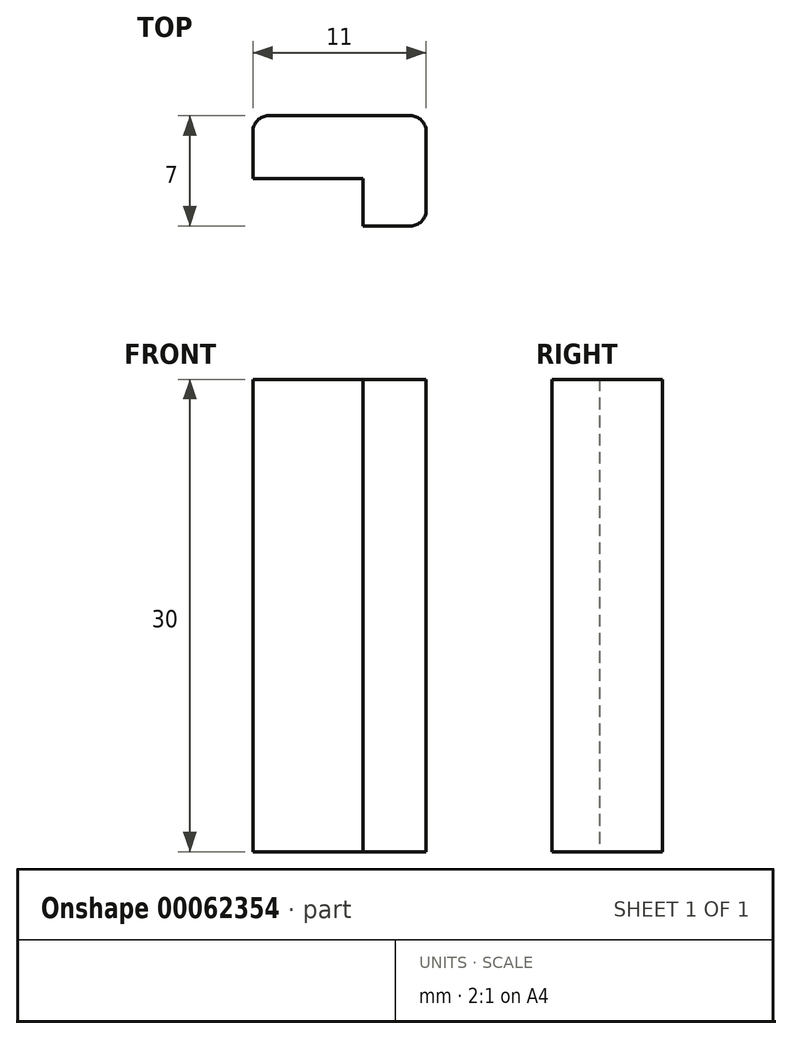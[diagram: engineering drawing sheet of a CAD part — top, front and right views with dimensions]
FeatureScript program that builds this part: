
annotation { "Feature Type Name" : "Feature", "Feature Type Description" : "" }
export const myFeature = defineFeature(function(context is Context, id is Id, definition is map)
    precondition{}
    {
        {
            var Q0;
            Q0=qCreatedBy(makeId("Top.planeOp"),FACE);
            var sketch = newSketch(context, id + "F0", { "sketchPlane" : qUnion([Q0])});
            skLineSegment(sketch, "E0", {"start": v(0, 0) * mm, "end": v(-7, 0) * mm});
            skLineSegment(sketch, "E1", {"start": v(-7, 0) * mm, "end": v(-7, 4) * mm});
            skLineSegment(sketch, "E2", {"start": v(-7, 4) * mm, "end": v(4, 4) * mm});
            skLineSegment(sketch, "E3", {"start": v(4, 4) * mm, "end": v(4, -3) * mm});
            skLineSegment(sketch, "E4", {"start": v(4, -3) * mm, "end": v(0, -3) * mm});
            skLineSegment(sketch, "E5", {"start": v(0, -3) * mm, "end": v(0, 0) * mm});
            skSolve(sketch);
        }
        {
            var Q0;
            Q0 = qSketchRegion(id + "F0", true);
            extrude(context, id + "F1", {"entities" : qUnion([Q0]), "depth" : 30 * mm});
        }
        {
            var Q0;
            Q0=makeQuery(id+"F1.opExtrude","SWEPT_EDGE",EDGE,{"disambiguationData":[OSD([sQuery(id+"F0.wireOp",EDGE,"E3"),sQuery(id+"F0.wireOp",EDGE,"E4")])]});
            var Q1;
            Q1=makeQuery(id+"F1.opExtrude","SWEPT_EDGE",EDGE,{"disambiguationData":[OSD([sQuery(id+"F0.wireOp",EDGE,"E1"),sQuery(id+"F0.wireOp",EDGE,"E2")])]});
            var Q2;
            Q2=makeQuery(id+"F1.opExtrude","SWEPT_EDGE",EDGE,{"disambiguationData":[OSD([sQuery(id+"F0.wireOp",EDGE,"E2"),sQuery(id+"F0.wireOp",EDGE,"E3")])]});
            fillet(context, id + "F2", {"entities" : qUnion([Q0, Q1, Q2]), "radius" : 1 * mm, "tangentPropagation" : true, "allowEdgeOverflow" : false});
        }
    });
